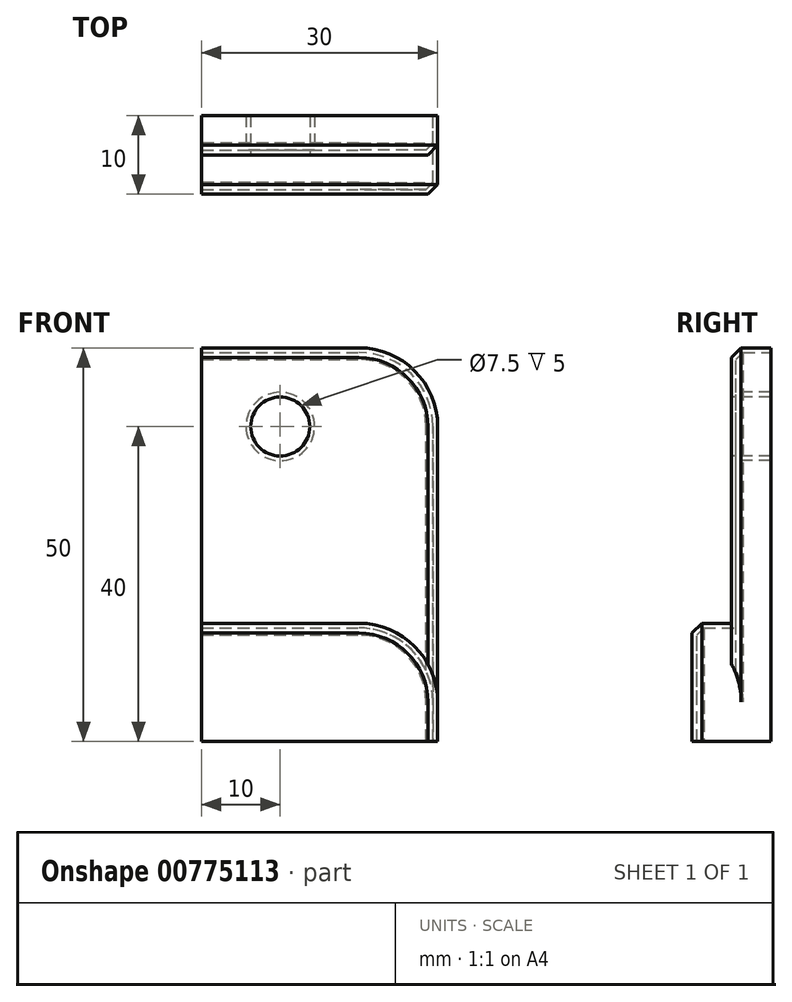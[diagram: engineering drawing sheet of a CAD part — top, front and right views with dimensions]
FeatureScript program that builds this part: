
annotation { "Feature Type Name" : "Feature", "Feature Type Description" : "" }
export const myFeature = defineFeature(function(context is Context, id is Id, definition is map)
    precondition{}
    {
        {
            var Q0;
            Q0=qCreatedBy(makeId("Front.planeOp"),FACE);
            var sketch = newSketch(context, id + "F0", { "sketchPlane" : qUnion([Q0])});
            skLineSegment(sketch, "E0.bottom", {"start": v(0, 0) * mm, "end": v(30, 0) * mm});
            skLineSegment(sketch, "E0.top", {"start": v(0, 50) * mm, "end": v(30, 50) * mm});
            skLineSegment(sketch, "E0.left", {"start": v(0, 0) * mm, "end": v(0, 50) * mm});
            skLineSegment(sketch, "E0.right", {"start": v(30, 0) * mm, "end": v(30, 50) * mm});
            skSolve(sketch);
        }
        {
            var Q0;
            Q0=makeQuery(id+"F0.imprint","IMPRINT",FACE,{"disambiguationData":[TD([[makeQuery(id+"F0.imprint","IMPRINT",EDGE,{"derivedFrom":sQuery(id+"F0.wireOp",EDGE,"E0.bottom")}),1.0]])]});
            extrude(context, id + "F1", {"entities" : qUnion([Q0]), "depth" : 5 * mm, "offsetDistance" : 25 * mm});
        }
        {
            var Q0;
            Q0=makeQuery(id+"F1.opExtrude","CAP_FACE",FACE,{"disambiguationData":[OSD([sQuery(id+"F0.wireOp",EDGE,"E0.bottom"),sQuery(id+"F0.wireOp",EDGE,"E0.top"),sQuery(id+"F0.wireOp",EDGE,"E0.left"),sQuery(id+"F0.wireOp",EDGE,"E0.right")])],"isStart":false});
            var sketch = newSketch(context, id + "F2", { "sketchPlane" : qUnion([Q0])});
            skLineSegment(sketch, "E1.bottom", {"start": v(0, 0) * mm, "end": v(30, 0) * mm});
            skLineSegment(sketch, "E1.top", {"start": v(0, 15) * mm, "end": v(30, 15) * mm});
            skLineSegment(sketch, "E1.left", {"start": v(0, 0) * mm, "end": v(0, 15) * mm});
            skLineSegment(sketch, "E1.right", {"start": v(30, 0) * mm, "end": v(30, 15) * mm});
            skSolve(sketch);
        }
        {
            var Q0;
            Q0=makeQuery(id+"F2.imprint","IMPRINT",FACE,{"disambiguationData":[TD([[makeQuery(id+"F2.imprint","IMPRINT",EDGE,{"derivedFrom":sQuery(id+"F2.wireOp",EDGE,"E1.bottom")}),1.0]])]});
            extrude(context, id + "F3", {"entities" : qUnion([Q0]), "operationType" : NewBodyOperationType.ADD, "depth" : 5 * mm, "offsetDistance" : 25 * mm});
        }
        {
            var Q0;
            Q0=makeQuery(id+"F1.opExtrude","CAP_FACE",FACE,{"disambiguationData":[OSD([sQuery(id+"F0.wireOp",EDGE,"E0.bottom"),sQuery(id+"F0.wireOp",EDGE,"E0.top"),sQuery(id+"F0.wireOp",EDGE,"E0.left"),sQuery(id+"F0.wireOp",EDGE,"E0.right")])],"isStart":false});
            var sketch = newSketch(context, id + "F4", { "sketchPlane" : qUnion([Q0])});
            skCircle(sketch, "E2", {"center": v(10, 40) * mm, "radius": 3.75 * mm});
            skSolve(sketch);
        }
        {
            var Q0;
            Q0=makeQuery(id+"F4.imprint","IMPRINT",FACE,{"disambiguationData":[TD([[makeQuery(id+"F4.imprint","IMPRINT",EDGE,{"derivedFrom":sQuery(id+"F4.wireOp",EDGE,"E2")}),1.0]])]});
            extrude(context, id + "F5", {"entities" : qUnion([Q0]), "operationType" : NewBodyOperationType.REMOVE, "endBound" : BoundingType.THROUGH_ALL, "oppositeDirection" : true, "depth" : 25 * mm, "offsetDistance" : 25 * mm});
        }
        {
            var Q0;
            Q0=makeQuery(id+"F1.opExtrude","SWEPT_EDGE",EDGE,{"disambiguationData":[OSD([sQuery(id+"F0.wireOp",EDGE,"E0.top"),sQuery(id+"F0.wireOp",EDGE,"E0.right")])]});
            var Q1;
            Q1=makeQuery(id+"F3.opExtrude","SWEPT_EDGE",EDGE,{"disambiguationData":[OSD([sQuery(id+"F0.wireOp",EDGE,"E0.right"),sQuery(id+"F2.wireOp",EDGE,"E1.top"),sQuery(id+"F2.wireOp",EDGE,"E1.right")])]});
            fillet(context, id + "F6", {"entities" : qUnion([Q0, Q1]), "radius" : 10 * mm, "tangentPropagation" : true, "allowEdgeOverflow" : false});
        }
        {
            var Q0;
            Q0=makeQuery(id+"F1.opExtrude","CAP_EDGE",EDGE,{"disambiguationData":[OSD([sQuery(id+"F0.wireOp",EDGE,"E0.top")])],"isStart":false});
            var Q1;
            Q1=makeQuery(id+"F3.opExtrude","CAP_EDGE",EDGE,{"disambiguationData":[OSD([sQuery(id+"F2.wireOp",EDGE,"E1.top")])],"isStart":false});
            chamfer(context, id + "F7", {"entities" : qUnion([Q0, Q1]), "width" : 1.25 * mm, "tangentPropagation" : true});
        }
        {
            var Q0;
            Q0=makeQuery(id+"F3.boolean.opBoolean","MERGE",FACE,{"derivedFrom":[makeQuery(id+"F1.opExtrude","SWEPT_FACE",FACE,{"disambiguationData":[OSD([sQuery(id+"F0.wireOp",EDGE,"E0.bottom")])]}),makeQuery(id+"F3.opExtrude","SWEPT_FACE",FACE,{"disambiguationData":[OSD([sQuery(id+"F2.wireOp",EDGE,"E1.bottom")])]})]});
            var Q1;
            Q1=makeQuery(id+"F3.boolean.opBoolean","MERGE",FACE,{"derivedFrom":[makeQuery(id+"F1.opExtrude","SWEPT_FACE",FACE,{"disambiguationData":[OSD([sQuery(id+"F0.wireOp",EDGE,"E0.left")])]}),makeQuery(id+"F3.opExtrude","SWEPT_FACE",FACE,{"disambiguationData":[OSD([sQuery(id+"F2.wireOp",EDGE,"E1.left")])]})]});
            var Q2;
            Q2=makeQuery(id+"F1.opExtrude","CAP_FACE",FACE,{"disambiguationData":[OSD([sQuery(id+"F0.wireOp",EDGE,"E0.bottom"),sQuery(id+"F0.wireOp",EDGE,"E0.top"),sQuery(id+"F0.wireOp",EDGE,"E0.left"),sQuery(id+"F0.wireOp",EDGE,"E0.right")])],"isStart":true});
            shell(context, id + "F8", {"entities" : qUnion([Q0, Q1, Q2]), "thickness" : 0.6 * mm});
        }
    });
